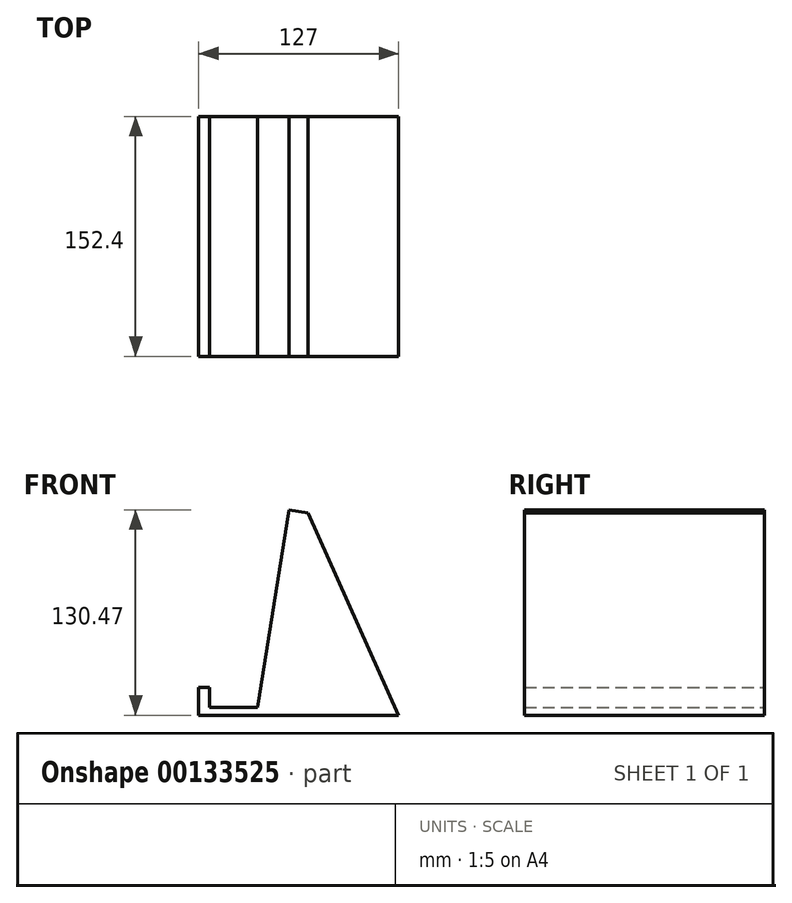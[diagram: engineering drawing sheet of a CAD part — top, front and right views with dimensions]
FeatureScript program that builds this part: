
annotation { "Feature Type Name" : "Feature", "Feature Type Description" : "" }
export const myFeature = defineFeature(function(context is Context, id is Id, definition is map)
    precondition{}
    {
        {
            var Q0;
            Q0=qCreatedBy(makeId("Front.planeOp"),FACE);
            var sketch = newSketch(context, id + "F0", { "sketchPlane" : qUnion([Q0])});
            skLineSegment(sketch, "E0", {"start": v(0, 0) * mm, "end": v(0, 17.78) * mm});
            skLineSegment(sketch, "E1", {"start": v(0, 17.78) * mm, "end": v(6.72, 17.78) * mm});
            skLineSegment(sketch, "E2", {"start": v(6.72, 17.78) * mm, "end": v(6.72, 5.08) * mm});
            skLineSegment(sketch, "E3", {"start": v(6.72, 5.08) * mm, "end": v(37.2, 5.08) * mm});
            skLineSegment(sketch, "E4", {"start": v(37.2, 5.08) * mm, "end": v(57.35, 130.47) * mm});
            skLineSegment(sketch, "E5", {"start": v(57.35, 130.47) * mm, "end": v(69.23, 128.56) * mm});
            skLineSegment(sketch, "E6", {"start": v(69.23, 128.56) * mm, "end": v(127, 0) * mm});
            skLineSegment(sketch, "E7", {"start": v(127, 0) * mm, "end": v(0, 0) * mm});
            skSolve(sketch);
        }
        {
            var Q0;
            Q0 = qSketchRegion(id + "F0", true);
            extrude(context, id + "F1", {"entities" : qUnion([Q0]), "depth" : 152.4 * mm});
        }
    });
